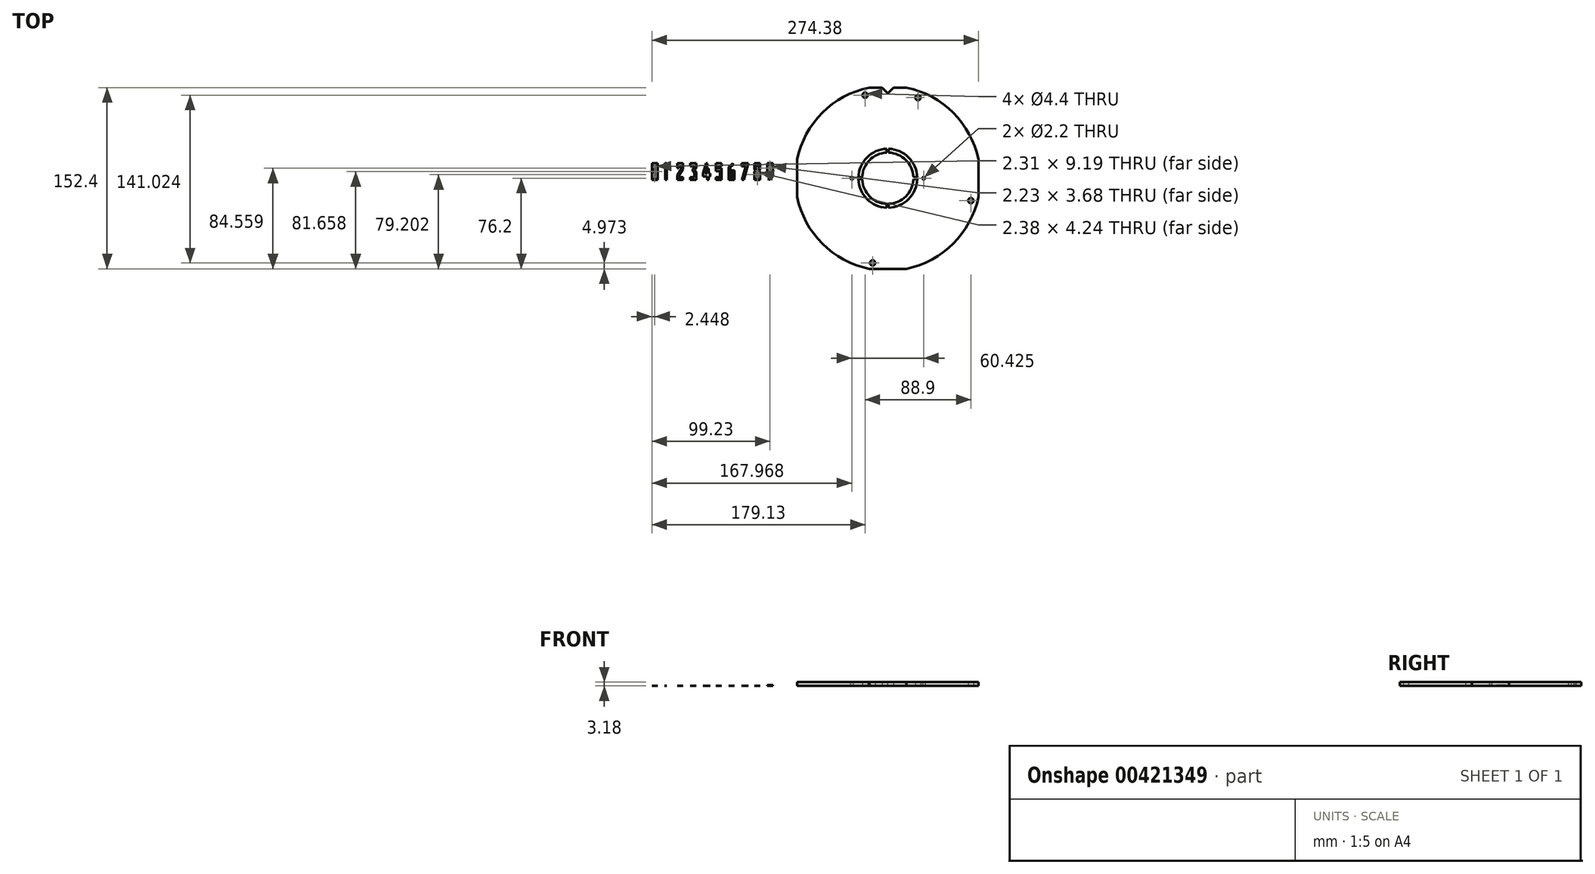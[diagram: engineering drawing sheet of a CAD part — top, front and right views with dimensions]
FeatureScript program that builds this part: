
annotation { "Feature Type Name" : "Feature", "Feature Type Description" : "" }
export const myFeature = defineFeature(function(context is Context, id is Id, definition is map)
    precondition{}
    {
        {
            var Q0;
            Q0=qCreatedBy(makeId("Top.planeOp"),FACE);
            var sketch = newSketch(context, id + "F0", { "sketchPlane" : qUnion([Q0])});
            skCircle(sketch, "E0", {"center": v(0, 0) * mm, "radius": 40.6 * mm, "construction": true});
            skCircle(sketch, "E1", {"center": v(0, 0) * mm, "radius": 72.35 * mm, "construction": true});
            skCircle(sketch, "E2", {"center": v(0, 0) * mm, "radius": 77.79 * mm});
            skLineSegment(sketch, "E3", {"start": v(0, 0) * mm, "end": v(-40.6, 0) * mm, "construction": true});
            skLineSegment(sketch, "E4", {"start": v(0, 0) * mm, "end": v(40.6, 0) * mm, "construction": true});
            skCircle(sketch, "E5", {"center": v(-30.21, 0) * mm, "radius": 1.1 * mm});
            skLineSegment(sketch, "E6", {"start": v(0, 0) * mm, "end": v(0, 15.28) * mm, "construction": true});
            skCircle(sketch, "E7.MirrorC", {"center": v(30.21, 0) * mm, "radius": 1.1 * mm});
            skCircle(sketch, "E8", {"center": v(-19.05, 69.8) * mm, "radius": 2.2 * mm});
            skCircle(sketch, "E9", {"center": v(25.4, 67.74) * mm, "radius": 2.2 * mm});
            skCircle(sketch, "E10", {"center": v(-12.7, -71.23) * mm, "radius": 2.2 * mm});
            skCircle(sketch, "E11", {"center": v(69.85, -18.85) * mm, "radius": 2.2 * mm});
            skSolve(sketch);
        }
        {
            var Q0;
            Q0=makeQuery(id+"F0.imprint","IMPRINT",FACE,{"disambiguationData":[TD([[makeQuery(id+"F0.imprint","IMPRINT",EDGE,{"derivedFrom":sQuery(id+"F0.wireOp",EDGE,"E2")}),1.0]])]});
            extrude(context, id + "F1", {"entities" : qUnion([Q0]), "depth" : 3.17 * mm, "offsetDistance" : 25.4 * mm});
        }
        {
            var Q0;
            Q0=makeQuery(id+"F1.opExtrude","CAP_FACE",FACE,{"disambiguationData":[OSD([sQuery(id+"F0.wireOp",EDGE,"E2"),sQuery(id+"F0.wireOp",EDGE,"E5"),sQuery(id+"F0.wireOp",EDGE,"E7.MirrorC"),sQuery(id+"F0.wireOp",EDGE,"E8"),sQuery(id+"F0.wireOp",EDGE,"E9"),sQuery(id+"F0.wireOp",EDGE,"E10"),sQuery(id+"F0.wireOp",EDGE,"E11")])],"isStart":false});
            var sketch = newSketch(context, id + "F2", { "sketchPlane" : qUnion([Q0])});
            skCircle(sketch, "E12.0", {"center": v(0, 0) * mm, "radius": 77.79 * mm});
            skLineSegment(sketch, "E13", {"start": v(0, 2.15) * mm, "end": v(0, 77.79) * mm, "construction": true});
            skLineSegment(sketch, "E14", {"start": v(0, 71.44) * mm, "end": v(-6.1, 77.55) * mm});
            skLineSegment(sketch, "E15.MirrorCS", {"start": v(0, 71.44) * mm, "end": v(6.1, 77.55) * mm});
            skSolve(sketch);
        }
        {
            var Q0;
            {var subQ0=sQuery(id+"F2.wireOp",EDGE,"E14");Q0=makeQuery(id+"F2.imprint","IMPRINT",FACE,{"disambiguationData":[TD([[makeQuery(id+"F2.imprint","IMPRINT",EDGE,{"derivedFrom":subQ0}),-1.0]])]});}
            var Q1;
            Q1=makeQuery(id+"F1.opExtrude","CAP_FACE",FACE,{"disambiguationData":[OSD([sQuery(id+"F0.wireOp",EDGE,"E2"),sQuery(id+"F0.wireOp",EDGE,"E5"),sQuery(id+"F0.wireOp",EDGE,"E7.MirrorC"),sQuery(id+"F0.wireOp",EDGE,"E8"),sQuery(id+"F0.wireOp",EDGE,"E9"),sQuery(id+"F0.wireOp",EDGE,"E10"),sQuery(id+"F0.wireOp",EDGE,"E11")])],"isStart":true});
            extrude(context, id + "F3", {"entities" : qUnion([Q0]), "operationType" : NewBodyOperationType.REMOVE, "endBound" : BoundingType.UP_TO_SURFACE, "oppositeDirection" : true, "endBoundEntityFace" : qUnion([Q1]), "depth" : 25.4 * mm});
        }
        {
            var Q0;
            Q0=makeQuery(id+"F1.opExtrude","CAP_FACE",FACE,{"disambiguationData":[OSD([sQuery(id+"F0.wireOp",EDGE,"E2"),sQuery(id+"F0.wireOp",EDGE,"E5"),sQuery(id+"F0.wireOp",EDGE,"E7.MirrorC"),sQuery(id+"F0.wireOp",EDGE,"E8"),sQuery(id+"F0.wireOp",EDGE,"E9"),sQuery(id+"F0.wireOp",EDGE,"E10"),sQuery(id+"F0.wireOp",EDGE,"E11")])],"isStart":false});
            var sketch = newSketch(context, id + "F4", { "sketchPlane" : qUnion([Q0])});
            skLineSegment(sketch, "E16", {"start": v(0, 0) * mm, "end": v(0, 71.44) * mm, "construction": true});
            skLineSegment(sketch, "E17", {"start": v(-77.79, 0) * mm, "end": v(77.79, 0) * mm, "construction": true});
            skArc(sketch, "E18", {"start": v(-0.8, 21.54) * mm, "mid": v(-15.24, 15.24) * mm, "end": v(-21.54, 0.8) * mm});
            skArc(sketch, "E19.0", {"start": v(-0.8, 24.71) * mm, "mid": v(-17.48, 17.48) * mm, "end": v(-24.71, 0.8) * mm});
            skLineSegment(sketch, "E20", {"start": v(-0.8, 24.71) * mm, "end": v(-0.8, 21.54) * mm});
            skLineSegment(sketch, "E21.MirrorCS", {"start": v(0.8, 24.71) * mm, "end": v(0.8, 21.54) * mm});
            skLineSegment(sketch, "E22.trimOffspring", {"start": v(-0.8, -21.54) * mm, "end": v(-0.8, -24.71) * mm});
            skLineSegment(sketch, "E23.trimOffspring", {"start": v(0.8, -21.54) * mm, "end": v(0.8, -24.71) * mm});
            skLineSegment(sketch, "E24", {"start": v(-24.71, 0.8) * mm, "end": v(-21.54, 0.8) * mm});
            skLineSegment(sketch, "E25.MirrorCS", {"start": v(-24.71, -0.8) * mm, "end": v(-21.54, -0.8) * mm});
            skLineSegment(sketch, "E26.trimOffspring", {"start": v(21.54, 0.8) * mm, "end": v(24.71, 0.8) * mm});
            skLineSegment(sketch, "E27.trimOffspring", {"start": v(21.54, -0.8) * mm, "end": v(24.71, -0.8) * mm});
            skArc(sketch, "E28.trimOffspring", {"start": v(-24.71, -0.8) * mm, "mid": v(-17.48, -17.48) * mm, "end": v(-0.8, -24.71) * mm});
            skArc(sketch, "E29.trimOffspring", {"start": v(-21.54, -0.8) * mm, "mid": v(-15.24, -15.24) * mm, "end": v(-0.8, -21.54) * mm});
            skArc(sketch, "E30.trimOffspring", {"start": v(21.54, 0.8) * mm, "mid": v(15.24, 15.24) * mm, "end": v(0.8, 21.54) * mm});
            skArc(sketch, "E31.trimOffspring", {"start": v(24.71, 0.8) * mm, "mid": v(17.48, 17.48) * mm, "end": v(0.8, 24.71) * mm});
            skArc(sketch, "E32.trimOffspring", {"start": v(0.8, -21.54) * mm, "mid": v(15.24, -15.24) * mm, "end": v(21.54, -0.8) * mm});
            skArc(sketch, "E33.trimOffspring", {"start": v(0.8, -24.71) * mm, "mid": v(17.48, -17.48) * mm, "end": v(24.71, -0.8) * mm});
            skSolve(sketch);
        }
        {
            var Q0;
            Q0 = qSketchRegion(id + "F4", true);
            extrude(context, id + "F5", {"entities" : qUnion([Q0]), "operationType" : NewBodyOperationType.REMOVE, "oppositeDirection" : true, "depth" : 1 / 812.8 * mm});
        }
        {
            var Q0;
            Q0=makeQuery(id+"F1.opExtrude","CAP_FACE",FACE,{"disambiguationData":[OSD([sQuery(id+"F0.wireOp",EDGE,"E2"),sQuery(id+"F0.wireOp",EDGE,"E5"),sQuery(id+"F0.wireOp",EDGE,"E7.MirrorC"),sQuery(id+"F0.wireOp",EDGE,"E8"),sQuery(id+"F0.wireOp",EDGE,"E9"),sQuery(id+"F0.wireOp",EDGE,"E10"),sQuery(id+"F0.wireOp",EDGE,"E11")])],"isStart":false});
            var sketch = newSketch(context, id + "F6", { "sketchPlane" : qUnion([Q0])});
            skLineSegment(sketch, "E34", {"start": v(0, 0) * mm, "end": v(-69.85, 0) * mm, "construction": true});
            skLineSegment(sketch, "E35", {"start": v(0, 0) * mm, "end": v(0, 30.88) * mm, "construction": true});
            skLineSegment(sketch, "E36.bottom", {"start": v(-34.93, 28.58) * mm, "end": v(-41.28, 28.58) * mm});
            skLineSegment(sketch, "E36.top", {"start": v(-34.92, -28.58) * mm, "end": v(-41.27, -28.58) * mm});
            skLineSegment(sketch, "E36.left", {"start": v(-34.93, 28.57) * mm, "end": v(-34.93, -28.58) * mm});
            skLineSegment(sketch, "E36.right", {"start": v(-41.28, 28.58) * mm, "end": v(-41.27, -28.58) * mm});
            skLineSegment(sketch, "E37.1.0.0", {"start": v(-53.98, 28.58) * mm, "end": v(-53.97, -28.58) * mm});
            skLineSegment(sketch, "E37.1.0.1", {"start": v(-47.63, 28.57) * mm, "end": v(-53.98, 28.57) * mm});
            skLineSegment(sketch, "E37.1.0.2", {"start": v(-47.63, 28.57) * mm, "end": v(-47.63, -28.58) * mm});
            skLineSegment(sketch, "E37.1.0.3", {"start": v(-47.62, -28.58) * mm, "end": v(-53.97, -28.58) * mm});
            skLineSegment(sketch, "E37.2.0.0", {"start": v(-66.68, 28.57) * mm, "end": v(-66.67, -28.58) * mm});
            skLineSegment(sketch, "E37.2.0.1", {"start": v(-60.33, 28.57) * mm, "end": v(-66.68, 28.57) * mm});
            skLineSegment(sketch, "E37.2.0.2", {"start": v(-60.33, 28.57) * mm, "end": v(-60.33, -28.58) * mm});
            skLineSegment(sketch, "E37.2.0.3", {"start": v(-60.32, -28.58) * mm, "end": v(-66.67, -28.58) * mm});
            skLineSegment(sketch, "E37.direction1", {"start": v(-41.27, -28.58) * mm, "end": v(-53.97, -28.58) * mm, "construction": true});
            skLineSegment(sketch, "E38.MirrorCS", {"start": v(60.32, -28.58) * mm, "end": v(66.67, -28.58) * mm});
            skLineSegment(sketch, "E39.MirrorCS", {"start": v(34.92, -28.58) * mm, "end": v(41.27, -28.58) * mm});
            skLineSegment(sketch, "E40.MirrorCS", {"start": v(34.93, 28.58) * mm, "end": v(41.28, 28.58) * mm});
            skLineSegment(sketch, "E41.MirrorCS", {"start": v(41.27, -28.58) * mm, "end": v(53.97, -28.58) * mm, "construction": true});
            skLineSegment(sketch, "E42.MirrorCS", {"start": v(60.33, 28.57) * mm, "end": v(66.68, 28.57) * mm});
            skLineSegment(sketch, "E43.MirrorCS", {"start": v(47.62, -28.58) * mm, "end": v(53.97, -28.58) * mm});
            skLineSegment(sketch, "E44.MirrorCS", {"start": v(47.63, 28.57) * mm, "end": v(53.98, 28.57) * mm});
            skLineSegment(sketch, "E45.MirrorCS", {"start": v(34.93, 28.57) * mm, "end": v(34.93, -28.58) * mm});
            skLineSegment(sketch, "E46.MirrorCS", {"start": v(41.28, 28.58) * mm, "end": v(41.27, -28.58) * mm});
            skLineSegment(sketch, "E47.MirrorCS", {"start": v(53.98, 28.58) * mm, "end": v(53.97, -28.58) * mm});
            skLineSegment(sketch, "E48.MirrorCS", {"start": v(60.33, 28.57) * mm, "end": v(60.33, -28.58) * mm});
            skLineSegment(sketch, "E49.MirrorCS", {"start": v(66.68, 28.57) * mm, "end": v(66.67, -28.58) * mm});
            skLineSegment(sketch, "E50.MirrorCS", {"start": v(47.63, 28.57) * mm, "end": v(47.63, -28.58) * mm});
            skSolve(sketch);
        }
        {
            var Q0;
            Q0=qCreatedBy(makeId("Top.planeOp"),FACE);
            var sketch = newSketch(context, id + "F7", { "sketchPlane" : qUnion([Q0])});
            skLineSegment(sketch, "E51", {"start": v(-185.71, 12.46) * mm, "end": v(-185.71, -1.5) * mm});
            skLineSegment(sketch, "E52", {"start": v(-185.71, -1.5) * mm, "end": v(-187.04, -1.5) * mm});
            skLineSegment(sketch, "E53", {"start": v(-187.04, -1.5) * mm, "end": v(-187.04, 10) * mm});
            skLineSegment(sketch, "E54", {"start": v(-187.04, 10) * mm, "end": v(-187.54, 10) * mm});
            skLineSegment(sketch, "E55", {"start": v(-187.54, 10) * mm, "end": v(-187.54, 11.93) * mm});
            skLineSegment(sketch, "E56", {"start": v(-187.54, 11.93) * mm, "end": v(-187.06, 12.46) * mm});
            skLineSegment(sketch, "E57", {"start": v(-187.06, 12.46) * mm, "end": v(-185.71, 12.46) * mm});
            skSolve(sketch);
        }
        {
            var Q0;
            Q0 = qSketchRegion(id + "F7", true);
            extrude(context, id + "F8", {"entities" : qUnion([Q0]), "depth" : 1 / 812.8 * mm});
        }
        {
            var Q0;
            Q0=qCreatedBy(makeId("Top.planeOp"),FACE);
            var sketch = newSketch(context, id + "F9", { "sketchPlane" : qUnion([Q0])});
            skLineSegment(sketch, "E58.bottom", {"start": v(-198.18, 12.44) * mm, "end": v(-193.3, 12.44) * mm});
            skLineSegment(sketch, "E58.top", {"start": v(-198.18, -1.52) * mm, "end": v(-193.3, -1.52) * mm});
            skLineSegment(sketch, "E58.left", {"start": v(-198.18, 12.44) * mm, "end": v(-198.18, -1.52) * mm});
            skLineSegment(sketch, "E58.right", {"start": v(-193.3, 12.44) * mm, "end": v(-193.3, -1.52) * mm});
            skLineSegment(sketch, "E59.bottom", {"start": v(-196.89, 10.05) * mm, "end": v(-194.58, 10.05) * mm});
            skLineSegment(sketch, "E59.top", {"start": v(-196.89, 0.87) * mm, "end": v(-194.58, 0.87) * mm});
            skLineSegment(sketch, "E59.left", {"start": v(-196.89, 10.05) * mm, "end": v(-196.89, 0.87) * mm});
            skLineSegment(sketch, "E59.right", {"start": v(-194.58, 10.05) * mm, "end": v(-194.58, 0.87) * mm});
            skSolve(sketch);
        }
        {
            var Q0;
            Q0 = qSketchRegion(id + "F9", true);
            extrude(context, id + "F10", {"entities" : qUnion([Q0]), "depth" : 1 / 812.8 * mm});
        }
        {
            var Q0;
            Q0=qCreatedBy(makeId("Top.planeOp"),FACE);
            var sketch = newSketch(context, id + "F11", { "sketchPlane" : qUnion([Q0])});
            skLineSegment(sketch, "E60", {"start": v(-176.7, 12.5) * mm, "end": v(-171.9, 12.5) * mm});
            skLineSegment(sketch, "E61", {"start": v(-171.9, 12.5) * mm, "end": v(-171.9, 7.69) * mm});
            skLineSegment(sketch, "E62", {"start": v(-171.9, 7.69) * mm, "end": v(-175.46, 2.05) * mm});
            skLineSegment(sketch, "E63", {"start": v(-175.46, 2.05) * mm, "end": v(-175.46, 0.94) * mm});
            skLineSegment(sketch, "E64", {"start": v(-175.46, 0.94) * mm, "end": v(-171.9, 0.94) * mm});
            skLineSegment(sketch, "E65", {"start": v(-171.9, 0.94) * mm, "end": v(-171.9, -1.51) * mm});
            skLineSegment(sketch, "E66", {"start": v(-171.9, -1.51) * mm, "end": v(-176.74, -1.51) * mm});
            skLineSegment(sketch, "E67", {"start": v(-176.74, -1.51) * mm, "end": v(-176.74, 2.45) * mm});
            skLineSegment(sketch, "E68", {"start": v(-176.74, 2.45) * mm, "end": v(-173.23, 7.88) * mm});
            skLineSegment(sketch, "E69", {"start": v(-173.23, 7.88) * mm, "end": v(-173.23, 10.01) * mm});
            skLineSegment(sketch, "E70", {"start": v(-173.23, 10.01) * mm, "end": v(-175.46, 10.01) * mm});
            skLineSegment(sketch, "E71", {"start": v(-175.46, 10.01) * mm, "end": v(-175.46, 8.6) * mm});
            skLineSegment(sketch, "E72", {"start": v(-175.46, 8.6) * mm, "end": v(-176.7, 8.6) * mm});
            skLineSegment(sketch, "E73", {"start": v(-176.7, 8.6) * mm, "end": v(-176.7, 12.5) * mm});
            skSolve(sketch);
        }
        {
            var Q0;
            Q0 = qSketchRegion(id + "F11", true);
            extrude(context, id + "F12", {"entities" : qUnion([Q0]), "depth" : 1 / 812.8 * mm});
        }
        {
            var Q0;
            Q0=qCreatedBy(makeId("Top.planeOp"),FACE);
            var sketch = newSketch(context, id + "F13", { "sketchPlane" : qUnion([Q0])});
            skLineSegment(sketch, "E74", {"start": v(-165.92, 12.5) * mm, "end": v(-161.08, 12.5) * mm});
            skLineSegment(sketch, "E75", {"start": v(-161.08, 12.5) * mm, "end": v(-161.08, 8.32) * mm});
            skLineSegment(sketch, "E76", {"start": v(-161.08, 8.32) * mm, "end": v(-162.61, 6.82) * mm});
            skLineSegment(sketch, "E77", {"start": v(-162.61, 6.82) * mm, "end": v(-161.08, 5.25) * mm});
            skLineSegment(sketch, "E78", {"start": v(-161.08, 5.25) * mm, "end": v(-161.08, -1.52) * mm});
            skLineSegment(sketch, "E79", {"start": v(-161.08, -1.52) * mm, "end": v(-165.92, -1.52) * mm});
            skLineSegment(sketch, "E80", {"start": v(-165.92, -1.52) * mm, "end": v(-165.92, 0.89) * mm});
            skLineSegment(sketch, "E81", {"start": v(-165.92, 0.89) * mm, "end": v(-162.37, 0.89) * mm});
            skLineSegment(sketch, "E82", {"start": v(-162.37, 0.89) * mm, "end": v(-162.37, 4.5) * mm});
            skLineSegment(sketch, "E83", {"start": v(-164.51, 6.8) * mm, "end": v(-162.37, 9.01) * mm});
            skLineSegment(sketch, "E84", {"start": v(-162.37, 9.01) * mm, "end": v(-162.37, 10.02) * mm});
            skLineSegment(sketch, "E85", {"start": v(-162.37, 10.02) * mm, "end": v(-165.92, 10.02) * mm});
            skLineSegment(sketch, "E86", {"start": v(-165.92, 10.02) * mm, "end": v(-165.92, 12.5) * mm});
            skLineSegment(sketch, "E87", {"start": v(-164.51, 6.8) * mm, "end": v(-162.37, 4.64) * mm});
            skLineSegment(sketch, "E88", {"start": v(-162.37, 4.64) * mm, "end": v(-162.37, 4.5) * mm});
            skSolve(sketch);
        }
        {
            var Q0;
            Q0 = qSketchRegion(id + "F13", true);
            extrude(context, id + "F14", {"entities" : qUnion([Q0]), "depth" : 1 / 812.8 * mm});
        }
        {
            var Q0;
            Q0=qCreatedBy(makeId("Top.planeOp"),FACE);
            var sketch = newSketch(context, id + "F15", { "sketchPlane" : qUnion([Q0])});
            skLineSegment(sketch, "E89", {"start": v(-152.82, 12.45) * mm, "end": v(-151.43, 12.45) * mm});
            skLineSegment(sketch, "E90", {"start": v(-151.43, 12.45) * mm, "end": v(-153.76, 3.9) * mm});
            skLineSegment(sketch, "E91", {"start": v(-153.76, 3.9) * mm, "end": v(-151.64, 3.9) * mm});
            skLineSegment(sketch, "E92", {"start": v(-151.64, 3.9) * mm, "end": v(-151.64, 8.3) * mm});
            skLineSegment(sketch, "E93", {"start": v(-151.64, 8.3) * mm, "end": v(-150.31, 8.3) * mm});
            skLineSegment(sketch, "E94", {"start": v(-150.31, 8.3) * mm, "end": v(-150.31, 3.9) * mm});
            skLineSegment(sketch, "E95", {"start": v(-150.31, 3.9) * mm, "end": v(-149.1, 3.9) * mm});
            skLineSegment(sketch, "E96", {"start": v(-149.1, 3.9) * mm, "end": v(-149.1, 1.39) * mm});
            skLineSegment(sketch, "E97", {"start": v(-149.1, 1.39) * mm, "end": v(-150.31, 1.39) * mm});
            skLineSegment(sketch, "E98", {"start": v(-150.31, 1.39) * mm, "end": v(-150.31, -1.48) * mm});
            skLineSegment(sketch, "E99", {"start": v(-150.31, -1.48) * mm, "end": v(-151.64, -1.48) * mm});
            skLineSegment(sketch, "E100", {"start": v(-151.64, -1.48) * mm, "end": v(-151.64, 1.39) * mm});
            skLineSegment(sketch, "E101", {"start": v(-151.64, 1.39) * mm, "end": v(-155.18, 1.39) * mm});
            skLineSegment(sketch, "E102", {"start": v(-155.18, 1.39) * mm, "end": v(-155.18, 3.9) * mm});
            skLineSegment(sketch, "E103", {"start": v(-155.18, 3.9) * mm, "end": v(-152.82, 12.45) * mm});
            skSolve(sketch);
        }
        {
            var Q0;
            Q0 = qSketchRegion(id + "F15", true);
            extrude(context, id + "F16", {"entities" : qUnion([Q0]), "depth" : 1 / 812.8 * mm});
        }
        {
            var Q0;
            Q0=qCreatedBy(makeId("Top.planeOp"),FACE);
            var sketch = newSketch(context, id + "F17", { "sketchPlane" : qUnion([Q0])});
            skLineSegment(sketch, "E104", {"start": v(-144.36, 12.48) * mm, "end": v(-139.51, 12.48) * mm});
            skLineSegment(sketch, "E105", {"start": v(-139.51, 12.48) * mm, "end": v(-139.51, 10.05) * mm});
            skLineSegment(sketch, "E106", {"start": v(-139.51, 10.05) * mm, "end": v(-143.1, 10.05) * mm});
            skLineSegment(sketch, "E107", {"start": v(-143.1, 10.05) * mm, "end": v(-143.1, 8.35) * mm});
            skLineSegment(sketch, "E108", {"start": v(-143.1, 8.35) * mm, "end": v(-139.51, 8.35) * mm});
            skLineSegment(sketch, "E109", {"start": v(-139.51, 8.35) * mm, "end": v(-139.51, -1.5) * mm});
            skLineSegment(sketch, "E110", {"start": v(-139.51, -1.5) * mm, "end": v(-144.36, -1.5) * mm});
            skLineSegment(sketch, "E111", {"start": v(-144.36, -1.5) * mm, "end": v(-144.36, 0.95) * mm});
            skLineSegment(sketch, "E112", {"start": v(-144.36, 0.95) * mm, "end": v(-140.79, 0.95) * mm});
            skLineSegment(sketch, "E113", {"start": v(-140.79, 0.95) * mm, "end": v(-140.79, 5.88) * mm});
            skLineSegment(sketch, "E114", {"start": v(-140.79, 5.88) * mm, "end": v(-144.36, 5.88) * mm});
            skLineSegment(sketch, "E115", {"start": v(-144.36, 5.88) * mm, "end": v(-144.36, 12.48) * mm});
            skSolve(sketch);
        }
        {
            var Q0;
            Q0 = qSketchRegion(id + "F17", true);
            extrude(context, id + "F18", {"entities" : qUnion([Q0]), "depth" : 1 / 812.8 * mm});
        }
        {
            var Q0;
            Q0=qCreatedBy(makeId("Top.planeOp"),FACE);
            var sketch = newSketch(context, id + "F19", { "sketchPlane" : qUnion([Q0])});
            skLineSegment(sketch, "E116", {"start": v(-132.4, 6.7) * mm, "end": v(-128.99, 6.7) * mm});
            skLineSegment(sketch, "E117", {"start": v(-128.99, 6.7) * mm, "end": v(-128.99, -1.52) * mm});
            skLineSegment(sketch, "E118", {"start": v(-128.99, -1.52) * mm, "end": v(-133.57, -1.52) * mm});
            skLineSegment(sketch, "E119", {"start": v(-133.57, -1.52) * mm, "end": v(-133.57, 9.56) * mm});
            skLineSegment(sketch, "E120", {"start": v(-133.57, 9.56) * mm, "end": v(-130.16, 12.53) * mm});
            skLineSegment(sketch, "E121", {"start": v(-130.16, 12.53) * mm, "end": v(-130.16, 10.9) * mm});
            skLineSegment(sketch, "E122", {"start": v(-130.16, 10.9) * mm, "end": v(-132.4, 8.95) * mm});
            skLineSegment(sketch, "E123", {"start": v(-132.4, 8.95) * mm, "end": v(-132.4, 6.7) * mm});
            skLineSegment(sketch, "E124.bottom", {"start": v(-132.4, 4.36) * mm, "end": v(-130.22, 4.36) * mm});
            skLineSegment(sketch, "E124.top", {"start": v(-132.4, 0.77) * mm, "end": v(-130.22, 0.77) * mm});
            skLineSegment(sketch, "E124.left", {"start": v(-132.4, 4.36) * mm, "end": v(-132.4, 0.77) * mm});
            skLineSegment(sketch, "E124.right", {"start": v(-130.22, 4.36) * mm, "end": v(-130.22, 0.77) * mm});
            skSolve(sketch);
        }
        {
            var Q0;
            Q0 = qSketchRegion(id + "F19", true);
            extrude(context, id + "F20", {"entities" : qUnion([Q0]), "depth" : 1 / 812.8 * mm});
        }
        {
            var Q0;
            Q0=qCreatedBy(makeId("Top.planeOp"),FACE);
            var sketch = newSketch(context, id + "F21", { "sketchPlane" : qUnion([Q0])});
            skLineSegment(sketch, "E125", {"start": v(-122.85, 10.06) * mm, "end": v(-122.85, 12.49) * mm});
            skLineSegment(sketch, "E126", {"start": v(-122.85, 12.49) * mm, "end": v(-117.23, 12.49) * mm});
            skLineSegment(sketch, "E127", {"start": v(-117.23, 12.49) * mm, "end": v(-121.09, -1.51) * mm});
            skLineSegment(sketch, "E128", {"start": v(-121.09, -1.51) * mm, "end": v(-122.44, -1.51) * mm});
            skLineSegment(sketch, "E129", {"start": v(-122.44, -1.51) * mm, "end": v(-119.25, 10.06) * mm});
            skLineSegment(sketch, "E130", {"start": v(-119.25, 10.06) * mm, "end": v(-122.85, 10.06) * mm});
            skSolve(sketch);
        }
        {
            var Q0;
            Q0 = qSketchRegion(id + "F21", true);
            extrude(context, id + "F22", {"entities" : qUnion([Q0]), "depth" : 1 / 812.8 * mm});
        }
        {
            var Q0;
            Q0=qCreatedBy(makeId("Top.planeOp"),FACE);
            var sketch = newSketch(context, id + "F23", { "sketchPlane" : qUnion([Q0])});
            skLineSegment(sketch, "E131", {"start": v(-112.04, 12.5) * mm, "end": v(-107.14, 12.5) * mm});
            skLineSegment(sketch, "E132", {"start": v(-107.14, 12.5) * mm, "end": v(-107.14, 7.15) * mm});
            skLineSegment(sketch, "E133", {"start": v(-107.14, 7.15) * mm, "end": v(-107.91, 6.35) * mm});
            skLineSegment(sketch, "E134", {"start": v(-107.91, 6.35) * mm, "end": v(-107.14, 5.6) * mm});
            skLineSegment(sketch, "E135", {"start": v(-107.14, 5.6) * mm, "end": v(-107.14, -1.52) * mm});
            skLineSegment(sketch, "E136", {"start": v(-107.14, -1.52) * mm, "end": v(-112.04, -1.52) * mm});
            skLineSegment(sketch, "E137", {"start": v(-112.04, -1.52) * mm, "end": v(-112.04, 5.6) * mm});
            skLineSegment(sketch, "E138", {"start": v(-112.04, 5.6) * mm, "end": v(-111.32, 6.35) * mm});
            skLineSegment(sketch, "E139", {"start": v(-112.04, 12.5) * mm, "end": v(-112.04, 7.15) * mm});
            skLineSegment(sketch, "E140", {"start": v(-112.04, 7.15) * mm, "end": v(-111.32, 6.35) * mm});
            skLineSegment(sketch, "E141.bottom", {"start": v(-110.75, 10.08) * mm, "end": v(-108.37, 10.08) * mm});
            skLineSegment(sketch, "E141.top", {"start": v(-110.75, 7.53) * mm, "end": v(-108.37, 7.53) * mm});
            skLineSegment(sketch, "E141.left", {"start": v(-110.75, 10.08) * mm, "end": v(-110.75, 7.53) * mm});
            skLineSegment(sketch, "E141.right", {"start": v(-108.37, 10.08) * mm, "end": v(-108.37, 7.53) * mm});
            skLineSegment(sketch, "E142.bottom", {"start": v(-110.75, 5.12) * mm, "end": v(-108.37, 5.12) * mm});
            skLineSegment(sketch, "E142.top", {"start": v(-110.75, 0.88) * mm, "end": v(-108.37, 0.88) * mm});
            skLineSegment(sketch, "E142.left", {"start": v(-110.75, 5.12) * mm, "end": v(-110.75, 0.88) * mm});
            skLineSegment(sketch, "E142.right", {"start": v(-108.37, 5.12) * mm, "end": v(-108.37, 0.88) * mm});
            skSolve(sketch);
        }
        {
            var Q0;
            Q0 = qSketchRegion(id + "F23", true);
            extrude(context, id + "F24", {"entities" : qUnion([Q0]), "depth" : 1 / 812.8 * mm});
        }
        {
            var Q0;
            Q0=qCreatedBy(makeId("Top.planeOp"),FACE);
            var sketch = newSketch(context, id + "F25", { "sketchPlane" : qUnion([Q0])});
            skLineSegment(sketch, "E143", {"start": v(-101.24, 12.48) * mm, "end": v(-96.62, 12.48) * mm});
            skLineSegment(sketch, "E144", {"start": v(-96.62, 12.48) * mm, "end": v(-96.62, 1.37) * mm});
            skLineSegment(sketch, "E145", {"start": v(-96.62, 1.37) * mm, "end": v(-100.13, -1.63) * mm});
            skLineSegment(sketch, "E146", {"start": v(-100.13, -1.63) * mm, "end": v(-100.13, 0) * mm});
            skLineSegment(sketch, "E147", {"start": v(-100.13, 0) * mm, "end": v(-97.88, 1.92) * mm});
            skLineSegment(sketch, "E148", {"start": v(-97.88, 1.92) * mm, "end": v(-97.88, 4.27) * mm});
            skLineSegment(sketch, "E149", {"start": v(-97.88, 4.27) * mm, "end": v(-101.24, 4.27) * mm});
            skLineSegment(sketch, "E150", {"start": v(-101.24, 4.27) * mm, "end": v(-101.24, 12.48) * mm});
            skLineSegment(sketch, "E151.bottom", {"start": v(-100.06, 10.2) * mm, "end": v(-97.83, 10.2) * mm});
            skLineSegment(sketch, "E151.top", {"start": v(-100.06, 6.52) * mm, "end": v(-97.83, 6.52) * mm});
            skLineSegment(sketch, "E151.left", {"start": v(-100.06, 10.2) * mm, "end": v(-100.06, 6.52) * mm});
            skLineSegment(sketch, "E151.right", {"start": v(-97.83, 10.2) * mm, "end": v(-97.83, 6.52) * mm});
            skSolve(sketch);
        }
        {
            var Q0;
            Q0 = qSketchRegion(id + "F25", true);
            extrude(context, id + "F26", {"entities" : qUnion([Q0]), "depth" : 0.8 * mm});
        }
        {
            var Q0;
            Q0=makeQuery(id+"F1.opExtrude","CAP_FACE",FACE,{"disambiguationData":[OSD([sQuery(id+"F0.wireOp",EDGE,"E2"),sQuery(id+"F0.wireOp",EDGE,"E5"),sQuery(id+"F0.wireOp",EDGE,"E7.MirrorC"),sQuery(id+"F0.wireOp",EDGE,"E8"),sQuery(id+"F0.wireOp",EDGE,"E9"),sQuery(id+"F0.wireOp",EDGE,"E10"),sQuery(id+"F0.wireOp",EDGE,"E11")])],"isStart":false});
            var sketch = newSketch(context, id + "F27", { "sketchPlane" : qUnion([Q0])});
            skLineSegment(sketch, "E152.bottom", {"start": v(-76.2, 76.2) * mm, "end": v(76.2, 76.2) * mm});
            skLineSegment(sketch, "E152.top", {"start": v(-76.2, -76.2) * mm, "end": v(76.2, -76.2) * mm});
            skLineSegment(sketch, "E152.left", {"start": v(-76.2, 76.2) * mm, "end": v(-76.2, -76.2) * mm});
            skLineSegment(sketch, "E152.right", {"start": v(76.2, 76.2) * mm, "end": v(76.2, -76.2) * mm});
            skPoint(sketch, "E152.middle", {"position": v(0, 0) * mm});
            skLineSegment(sketch, "E153.0", {"start": v(-82.55, 82.55) * mm, "end": v(-82.55, -82.55) * mm});
            skLineSegment(sketch, "E153.1", {"start": v(-82.55, 82.55) * mm, "end": v(82.55, 82.55) * mm});
            skLineSegment(sketch, "E153.2", {"start": v(82.55, 82.55) * mm, "end": v(82.55, -82.55) * mm});
            skLineSegment(sketch, "E153.3", {"start": v(-82.55, -82.55) * mm, "end": v(82.55, -82.55) * mm});
            skSolve(sketch);
        }
        {
            var Q0;
            Q0 = qSketchRegion(id + "F27", true);
            extrude(context, id + "F28", {"entities" : qUnion([Q0]), "operationType" : NewBodyOperationType.REMOVE, "oppositeDirection" : true, "depth" : 25.4 * mm});
        }
    });
